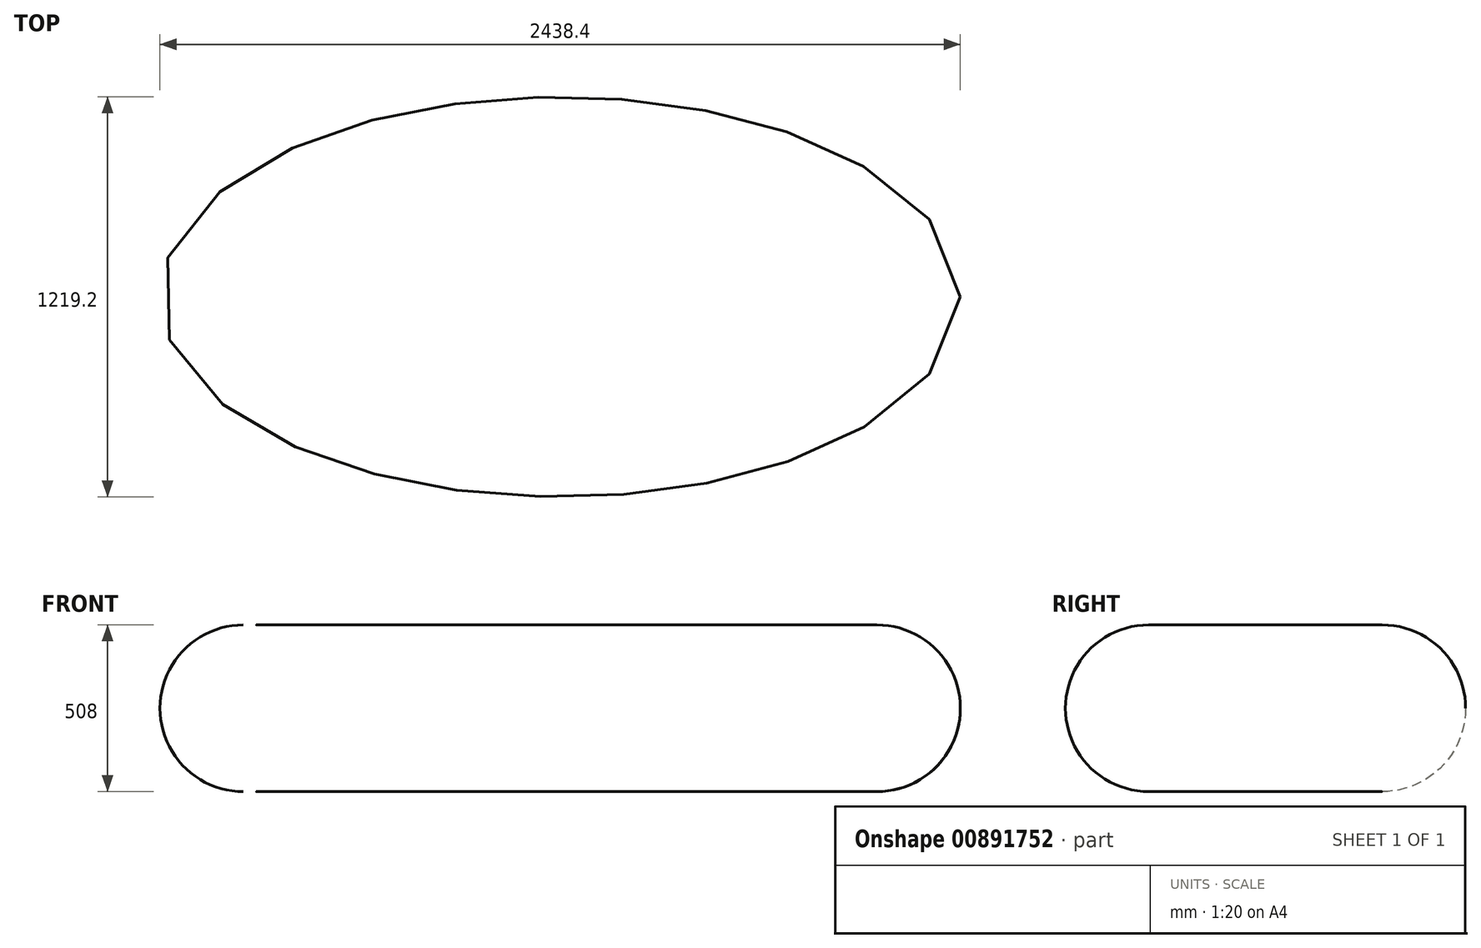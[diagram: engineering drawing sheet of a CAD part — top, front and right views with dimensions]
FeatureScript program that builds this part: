
annotation { "Feature Type Name" : "Feature", "Feature Type Description" : "" }
export const myFeature = defineFeature(function(context is Context, id is Id, definition is map)
    precondition{}
    {
        {
            var Q0;
            Q0=qCreatedBy(makeId("Top.planeOp"),FACE);
            var sketch = newSketch(context, id + "F0", { "sketchPlane" : qUnion([Q0])});
            skLineSegment(sketch, "E0", {"start": v(-1219.2, 0) * mm, "end": v(1219.2, 0) * mm, "construction": true});
            skLineSegment(sketch, "E1", {"start": v(0, 609.6) * mm, "end": v(0, -609.6) * mm, "construction": true});
            skEllipse(sketch, "E2", {"center": v(0, 0) * mm, "majorRadius": 1219.2 * mm, "minorRadius": 609.6 * mm, "majorAxis": v(1, 0)});
            skSolve(sketch);
        }
        {
            var Q0;
            Q0=makeQuery(id+"F0.imprint","IMPRINT",FACE,{"disambiguationData":[TD([[makeQuery(id+"F0.imprint","IMPRINT",EDGE,{"derivedFrom":sQuery(id+"F0.wireOp",EDGE,"E2")}),1.0]])]});
            extrude(context, id + "F1", {"entities" : qUnion([Q0]), "depth" : 508 * mm, "offsetDistance" : 25.4 * mm});
        }
        {
            var Q0;
            Q0=makeQuery(id+"F1.opExtrude","CAP_EDGE",EDGE,{"disambiguationData":[OSD([sQuery(id+"F0.wireOp",EDGE,"E2")])],"isStart":true});
            var Q1;
            Q1=makeQuery(id+"F1.opExtrude","CAP_EDGE",EDGE,{"disambiguationData":[OSD([sQuery(id+"F0.wireOp",EDGE,"E2")])],"isStart":false});
            fillet(context, id + "F2", {"entities" : qUnion([Q0, Q1]), "radius" : 254 * mm, "tangentPropagation" : true, "allowEdgeOverflow" : false});
        }
    });
